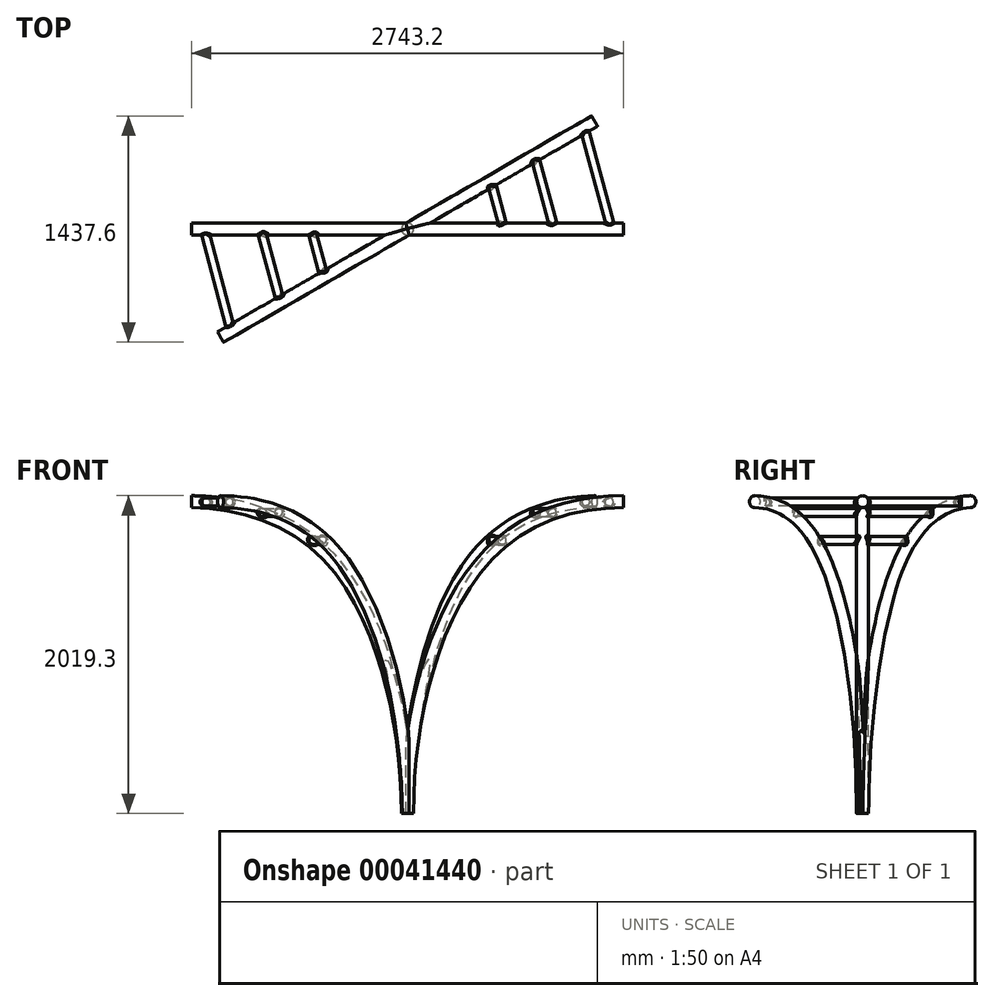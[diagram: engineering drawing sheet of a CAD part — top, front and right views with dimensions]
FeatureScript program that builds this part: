
annotation { "Feature Type Name" : "Feature", "Feature Type Description" : "" }
export const myFeature = defineFeature(function(context is Context, id is Id, definition is map)
    precondition{}
    {
        {
            var Q0;
            Q0=qCreatedBy(makeId("Front.planeOp"),FACE);
            var sketch = newSketch(context, id + "F0", { "sketchPlane" : qUnion([Q0])});
            skLineSegment(sketch, "E0", {"start": v(0, 297.55) * mm, "end": v(0, 0) * mm});
            skSolve(sketch);
        }
        {
            var Q0;
            Q0=qCreatedBy(makeId("Front.planeOp"),FACE);
            var sketch = newSketch(context, id + "F8", { "sketchPlane" : qUnion([Q0])});
            skLineSegment(sketch, "E1", {"start": v(0, 0) * mm, "end": v(0, 1981.2) * mm, "construction": true});
            skLineSegment(sketch, "E2", {"start": v(0, 1981.2) * mm, "end": v(-1371.6, 1981.2) * mm, "construction": true});
            skLineSegment(sketch, "E3", {"start": v(0, 1631.2) * mm, "end": v(-500, 1631.2) * mm, "construction": true});
            skFitSpline(sketch, "E4", {"points": [v(0, 0) * mm, v(-500, 1631.2) * mm, v(-1371.6, 1981.2) * mm], "startDerivative": vector(0, 2994.42) * mm, "endDerivative": vector(-1862.18, 0) * mm});
            skSolve(sketch);
        }
        {
            var Q0;
            Q0=qCreatedBy(makeId("Front.planeOp"),FACE);
            var Q1;
            Q1=sQuery(id+"F8.wireOp",EDGE,"E1");
            cPlane(context, id + "F1", {"entities" : qUnion([Q0, Q1]), "cplaneType" : CPlaneType.LINE_ANGLE, "offset" : 150 * mm, "angle" : 30 * degree, "width" : 150 * mm, "height" : 150 * mm});
        }
        {
            var Q0;
            Q0=qCreatedBy(id+"F1.planeOp",FACE);
            var sketch = newSketch(context, id + "F2", { "sketchPlane" : qUnion([Q0])});
            skLineSegment(sketch, "E5", {"start": v(0, 0) * mm, "end": v(0, 1981.2) * mm, "construction": true});
            skLineSegment(sketch, "E6", {"start": v(0, 1981.2) * mm, "end": v(1371.6, 1981.2) * mm, "construction": true});
            skLineSegment(sketch, "E7", {"start": v(0, 1631.2) * mm, "end": v(500, 1631.2) * mm, "construction": true});
            skFitSpline(sketch, "E8", {"points": [v(0, 0) * mm, v(500, 1631.2) * mm, v(1371.6, 1981.2) * mm], "startDerivative": vector(0, 3462.6) * mm, "endDerivative": vector(2329.76, 0) * mm});
            skSolve(sketch);
        }
        {
            var Q0;
            Q0=qCreatedBy(makeId("Top.planeOp"),FACE);
            var sketch = newSketch(context, id + "F3", { "sketchPlane" : qUnion([Q0])});
            skCircle(sketch, "E9", {"center": v(0, 0) * mm, "radius": 38.1 * mm});
            skSolve(sketch);
        }
        {
            var Q0;
            Q0 = qSketchRegion(id + "F3", true);
            var Q1;
            Q1=sQuery(id+"F2.wireOp",EDGE,"E8");
            sweep(context, id + "F4", {"profiles" : qUnion([Q0]), "path" : qUnion([Q1])});
        }
        {
            var Q0;
            Q0 = qSketchRegion(id + "F3", true);
            var Q1;
            Q1=sQuery(id+"F8.wireOp",EDGE,"E4");
            sweep(context, id + "F9", {"operationType" : NewBodyOperationType.ADD, "profiles" : qUnion([Q0]), "path" : qUnion([Q1])});
        }
        {
            var Q0;
            Q0=qCreatedBy(id+"F1.planeOp",FACE);
            var Q1;
            Q1=qCreatedBy(makeId("Front.planeOp"),FACE);
            cPlane(context, id + "F5", {"entities" : qUnion([Q0, Q1]), "cplaneType" : CPlaneType.MID_PLANE, "offset" : 150 * mm, "width" : 150 * mm, "height" : 150 * mm});
        }
        {
            var Q0;
            Q0=qCreatedBy(id+"F5.planeOp",FACE);
            var sketch = newSketch(context, id + "F10", { "sketchPlane" : qUnion([Q0])});
            skCircle(sketch, "E10", {"center": v(1248.69, 1979.32) * mm, "radius": 25.4 * mm});
            skCircle(sketch, "E11", {"center": v(590.74, 1736.07) * mm, "radius": 25.4 * mm});
            skCircle(sketch, "E12", {"center": v(899.39, 1912.67) * mm, "radius": 25.4 * mm});
            skFitSpline(sketch, "E13.0", {"points": [v(0, 0) * mm, v(0, 662.58) * mm, v(310.1, 1754.68) * mm, v(1005.36, 1981.2) * mm, v(1324.86, 1981.2) * mm], "construction": true});
            skLineSegment(sketch, "E14", {"start": v(1248.69, 1979.32) * mm, "end": v(899.39, 1912.67) * mm, "construction": true});
            skLineSegment(sketch, "E15", {"start": v(590.74, 1736.07) * mm, "end": v(899.39, 1912.67) * mm, "construction": true});
            skSolve(sketch);
        }
        {
            var Q0;
            Q0 = qSketchRegion(id + "F10", true);
            extrude(context, id + "F11", {"entities" : qUnion([Q0]), "operationType" : NewBodyOperationType.ADD, "endBound" : BoundingType.UP_TO_NEXT, "depth" : 1037.13 * mm, "hasSecondDirection" : true, "secondDirectionBound" : SecondDirectionBoundingType.UP_TO_NEXT, "secondDirectionOppositeDirection" : true, "secondDirectionDepth" : 25 * mm});
        }
        {
            var Q0;
            Q0=makeQuery(id+"F11.opExtrude","SWEPT_FACE",FACE,{"disambiguationData":[OSD([sQuery(id+"F10.wireOp",EDGE,"E10")])]});
            var Q1;
            Q1=makeQuery(id+"F11.opExtrude","SWEPT_FACE",FACE,{"disambiguationData":[OSD([sQuery(id+"F10.wireOp",EDGE,"E12")])]});
            var Q2;
            Q2=makeQuery(id+"F11.opExtrude","SWEPT_FACE",FACE,{"disambiguationData":[OSD([sQuery(id+"F10.wireOp",EDGE,"E11")])]});
            fillet(context, id + "F12", {"entities" : qUnion([Q0, Q1, Q2]), "radius" : 12 * mm, "tangentPropagation" : true, "allowEdgeOverflow" : false});
        }
        {
            var Q0;
            Q0=qCreatedBy(id+"F5.planeOp",FACE);
            var Q1;
            Q1=sQuery(id+"F0.wireOp",EDGE,"E0");
            cPlane(context, id + "F6", {"entities" : qUnion([Q0, Q1]), "cplaneType" : CPlaneType.LINE_ANGLE, "offset" : 150 * mm, "angle" : 90 * degree, "width" : 150 * mm, "height" : 150 * mm});
        }
        {
            var Q0;
            Q0=makeQuery(id+"F4.opSweep","SWEPT_BODY",BODY,{"disambiguationData":[OSD([sQuery(id+"F2.wireOp",EDGE,"E8"),sQuery(id+"F3.wireOp",EDGE,"E9")])]});
            var Q1;
            Q1=qCreatedBy(id+"F6.planeOp",FACE);
            mirror(context, id + "F13", {"operationType" : NewBodyOperationType.ADD, "entities" : qUnion([Q0]), "mirrorPlane" : qUnion([Q1])});
        }
    });
